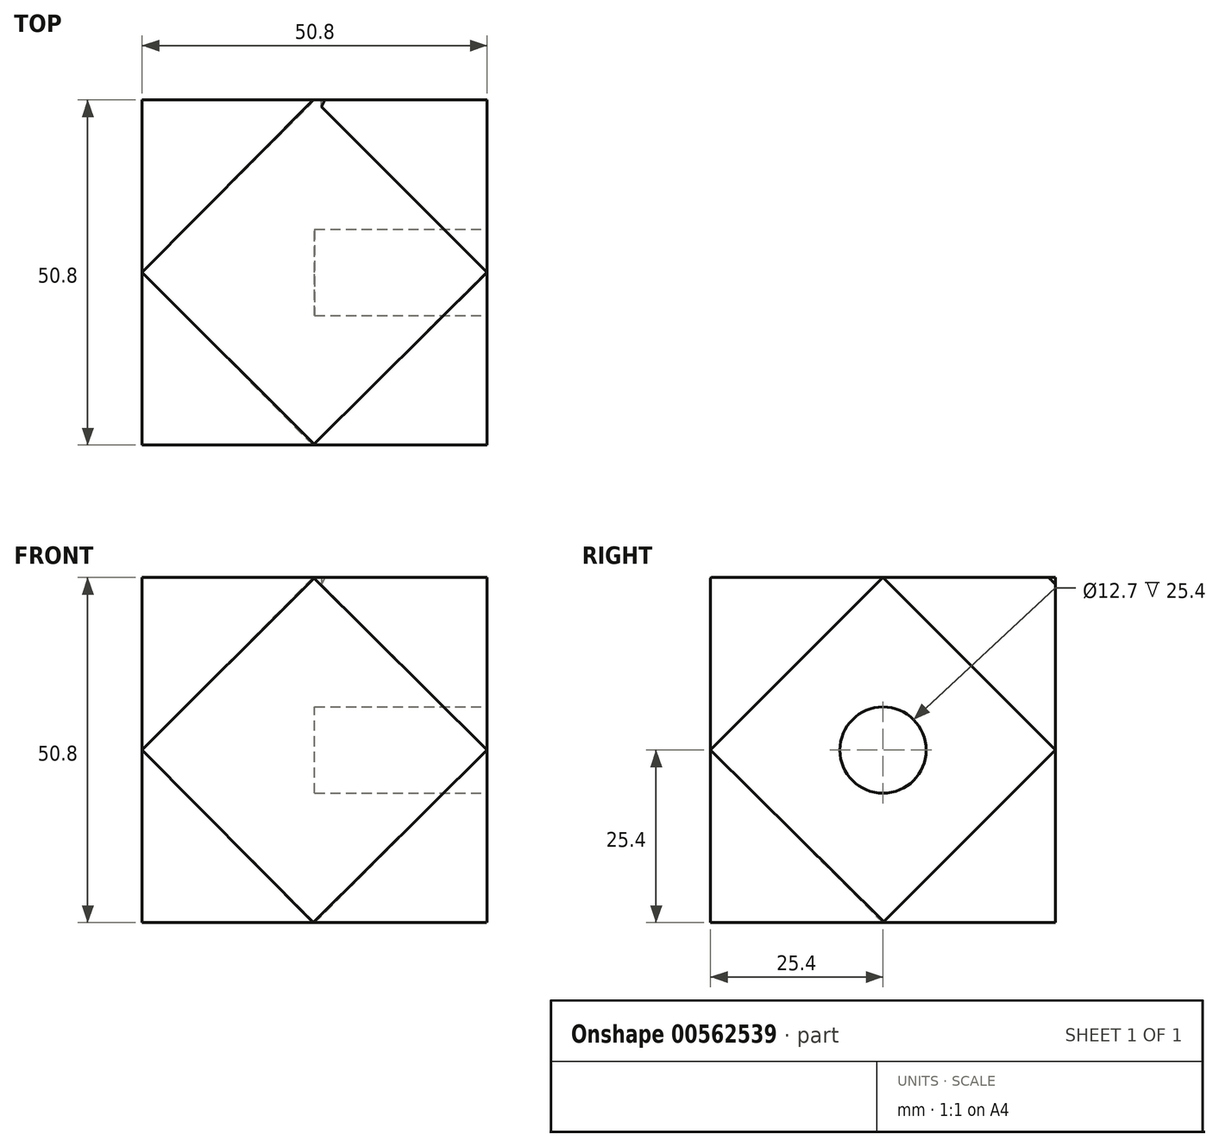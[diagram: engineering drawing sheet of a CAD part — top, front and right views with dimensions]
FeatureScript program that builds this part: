
annotation { "Feature Type Name" : "Feature", "Feature Type Description" : "" }
export const myFeature = defineFeature(function(context is Context, id is Id, definition is map)
    precondition{}
    {
        {
            var Q0;
            Q0=qCreatedBy(makeId("Front.planeOp"),FACE);
            var sketch = newSketch(context, id + "F0", { "sketchPlane" : qUnion([Q0])});
            skLineSegment(sketch, "E0.bottom", {"start": v(-25.15, 0) * mm, "end": v(25.65, 0) * mm});
            skLineSegment(sketch, "E0.top", {"start": v(-25.15, 50.8) * mm, "end": v(25.65, 50.8) * mm});
            skLineSegment(sketch, "E0.left", {"start": v(-25.15, 0) * mm, "end": v(-25.15, 50.8) * mm});
            skLineSegment(sketch, "E0.right", {"start": v(25.65, 0) * mm, "end": v(25.65, 50.8) * mm});
            skSolve(sketch);
        }
        {
            var Q0;
            Q0 = qSketchRegion(id + "F0", true);
            extrude(context, id + "F1", {"entities" : qUnion([Q0]), "endBound" : BoundingType.SYMMETRIC, "depth" : 50.8 * mm, "offsetDistance" : 25 * mm});
        }
        {
            var Q0;
            Q0=makeQuery(id+"F1.opExtrude","CAP_FACE",FACE,{"disambiguationData":[OSD([sQuery(id+"F0.wireOp",EDGE,"E0.bottom"),sQuery(id+"F0.wireOp",EDGE,"E0.top"),sQuery(id+"F0.wireOp",EDGE,"E0.left"),sQuery(id+"F0.wireOp",EDGE,"E0.right")])],"isStart":false});
            var sketch = newSketch(context, id + "F2", { "sketchPlane" : qUnion([Q0])});
            skLineSegment(sketch, "E1", {"start": v(25.65, 25.4) * mm, "end": v(0, 50.8) * mm});
            skLineSegment(sketch, "E2", {"start": v(0, 50.8) * mm, "end": v(-25.15, 25.4) * mm});
            skLineSegment(sketch, "E3", {"start": v(-25.15, 25.4) * mm, "end": v(0, 0) * mm});
            skLineSegment(sketch, "E4", {"start": v(0, 0) * mm, "end": v(25.65, 25.4) * mm});
            skSolve(sketch);
        }
        {
            var Q0;
            Q0=makeQuery(id+"F1.opExtrude","SWEPT_FACE",FACE,{"disambiguationData":[OSD([sQuery(id+"F0.wireOp",EDGE,"E0.right")])]});
            var sketch = newSketch(context, id + "F3", { "sketchPlane" : qUnion([Q0])});
            skLineSegment(sketch, "E5", {"start": v(0, 50.8) * mm, "end": v(-25.4, 25.4) * mm});
            skLineSegment(sketch, "E6", {"start": v(-25.4, 25.4) * mm, "end": v(0, 0) * mm});
            skLineSegment(sketch, "E7", {"start": v(0, 0) * mm, "end": v(25.4, 25.4) * mm});
            skLineSegment(sketch, "E8", {"start": v(25.4, 25.4) * mm, "end": v(0, 50.8) * mm});
            skSolve(sketch);
        }
        {
            var Q0;
            Q0=makeQuery(id+"F1.opExtrude","CAP_FACE",FACE,{"disambiguationData":[OSD([sQuery(id+"F0.wireOp",EDGE,"E0.bottom"),sQuery(id+"F0.wireOp",EDGE,"E0.top"),sQuery(id+"F0.wireOp",EDGE,"E0.left"),sQuery(id+"F0.wireOp",EDGE,"E0.right")])],"isStart":true});
            var sketch = newSketch(context, id + "F4", { "sketchPlane" : qUnion([Q0])});
            skLineSegment(sketch, "E9", {"start": v(0, 50.8) * mm, "end": v(-25.65, 25.4) * mm});
            skLineSegment(sketch, "E10", {"start": v(-25.65, 25.4) * mm, "end": v(0, 0) * mm});
            skLineSegment(sketch, "E11", {"start": v(0, 0) * mm, "end": v(25.15, 25.4) * mm});
            skLineSegment(sketch, "E12", {"start": v(25.15, 25.4) * mm, "end": v(0, 50.8) * mm});
            skSolve(sketch);
        }
        {
            var Q0;
            Q0=makeQuery(id+"F1.opExtrude","SWEPT_FACE",FACE,{"disambiguationData":[OSD([sQuery(id+"F0.wireOp",EDGE,"E0.left")])]});
            var sketch = newSketch(context, id + "F5", { "sketchPlane" : qUnion([Q0])});
            skLineSegment(sketch, "E13", {"start": v(-25.4, 25.4) * mm, "end": v(0, 50.8) * mm});
            skLineSegment(sketch, "E14", {"start": v(0, 50.8) * mm, "end": v(25.4, 25.4) * mm});
            skLineSegment(sketch, "E15", {"start": v(25.4, 25.4) * mm, "end": v(0, 0) * mm});
            skLineSegment(sketch, "E16", {"start": v(0, 0) * mm, "end": v(-25.4, 25.4) * mm});
            skSolve(sketch);
        }
        {
            var Q0;
            Q0=makeQuery(id+"F1.opExtrude","SWEPT_FACE",FACE,{"disambiguationData":[OSD([sQuery(id+"F0.wireOp",EDGE,"E0.top")])]});
            var sketch = newSketch(context, id + "F6", { "sketchPlane" : qUnion([Q0])});
            skLineSegment(sketch, "E17", {"start": v(-25.15, 0) * mm, "end": v(0.25, 25.4) * mm});
            skLineSegment(sketch, "E18", {"start": v(0.25, 25.4) * mm, "end": v(25.65, 0) * mm});
            skLineSegment(sketch, "E19", {"start": v(25.65, 0) * mm, "end": v(0.25, -25.4) * mm});
            skLineSegment(sketch, "E20", {"start": v(0.25, -25.4) * mm, "end": v(-25.15, 0) * mm});
            skSolve(sketch);
        }
        {
            var Q0;
            Q0=makeQuery(id+"F1.opExtrude","SWEPT_FACE",FACE,{"disambiguationData":[OSD([sQuery(id+"F0.wireOp",EDGE,"E0.bottom")])]});
            var sketch = newSketch(context, id + "F7", { "sketchPlane" : qUnion([Q0])});
            skLineSegment(sketch, "E21", {"start": v(-25.15, 0) * mm, "end": v(0.25, 25.4) * mm});
            skLineSegment(sketch, "E22", {"start": v(0.25, 25.4) * mm, "end": v(25.65, 0) * mm});
            skLineSegment(sketch, "E23", {"start": v(25.65, 0) * mm, "end": v(0.25, -25.4) * mm});
            skLineSegment(sketch, "E24", {"start": v(0.25, -25.4) * mm, "end": v(-25.15, 0) * mm});
            skSolve(sketch);
        }
        {
            var Q0;
            Q0=sQuery(id+"F7.wireOp",EDGE,"E24");
            var Q1;
            Q1=sQuery(id+"F5.wireOp",EDGE,"E16");
            cPlane(context, id + "F8", {"entities" : qUnion([Q0, Q1]), "cplaneType" : CPlaneType.LINE_ANGLE, "offset" : 25 * mm, "angle" : 0 * degree, "width" : 150 * mm, "height" : 150 * mm});
        }
        {
            var Q0;
            Q0=qCreatedBy(id+"F8.planeOp",FACE);
            var sketch = newSketch(context, id + "F9", { "sketchPlane" : qUnion([Q0])});
            skLineSegment(sketch, "E25.bottom", {"start": v(30.6, -24.4) * mm, "end": v(-50.97, -24.4) * mm});
            skLineSegment(sketch, "E25.top", {"start": v(30.6, 46.24) * mm, "end": v(-50.97, 46.24) * mm});
            skLineSegment(sketch, "E25.left", {"start": v(30.6, -24.4) * mm, "end": v(30.6, 46.24) * mm});
            skLineSegment(sketch, "E25.right", {"start": v(-50.97, -24.4) * mm, "end": v(-50.97, 46.24) * mm});
            skSolve(sketch);
        }
        {
            var Q0;
            Q0 = qSketchRegion(id + "F9", true);
            extrude(context, id + "F10", {"entities" : qUnion([Q0]), "operationType" : NewBodyOperationType.REMOVE, "depth" : 29.3 * mm, "offsetDistance" : 25 * mm});
        }
        {
            var Q0;
            Q0=sQuery(id+"F3.wireOp",EDGE,"E7");
            var Q1;
            Q1=sQuery(id+"F7.wireOp",EDGE,"E23");
            cPlane(context, id + "F11", {"entities" : qUnion([Q0, Q1]), "cplaneType" : CPlaneType.LINE_ANGLE, "offset" : 25 * mm, "angle" : 0 * degree, "width" : 150 * mm, "height" : 150 * mm});
        }
        {
            var Q0;
            Q0=qCreatedBy(id+"F11.planeOp",FACE);
            var sketch = newSketch(context, id + "F12", { "sketchPlane" : qUnion([Q0])});
            skCircle(sketch, "E26", {"center": v(-35.5, 68) * mm, "radius": 89.54 * mm});
            skSolve(sketch);
        }
        {
            var Q0;
            Q0 = qSketchRegion(id + "F12", true);
            extrude(context, id + "F13", {"entities" : qUnion([Q0]), "operationType" : NewBodyOperationType.REMOVE, "oppositeDirection" : true, "depth" : 25 * mm, "offsetDistance" : 25 * mm});
        }
        {
            var Q0;
            Q0=sQuery(id+"F6.wireOp",EDGE,"E18");
            var Q1;
            Q1=sQuery(id+"F3.wireOp",EDGE,"E8");
            cPlane(context, id + "F14", {"entities" : qUnion([Q0, Q1]), "cplaneType" : CPlaneType.LINE_ANGLE, "offset" : 25 * mm, "angle" : 0 * degree, "width" : 150 * mm, "height" : 150 * mm});
        }
        {
            var Q0;
            Q0=qCreatedBy(id+"F14.planeOp",FACE);
            var sketch = newSketch(context, id + "F15", { "sketchPlane" : qUnion([Q0])});
            skCircle(sketch, "E27", {"center": v(9.89, 17.48) * mm, "radius": 39.57 * mm});
            skSolve(sketch);
        }
        {
            var Q0;
            Q0 = qSketchRegion(id + "F15", true);
            extrude(context, id + "F16", {"entities" : qUnion([Q0]), "operationType" : NewBodyOperationType.REMOVE, "oppositeDirection" : true, "depth" : 41 * mm, "offsetDistance" : 25 * mm});
        }
        {
            var Q0;
            Q0=sQuery(id+"F5.wireOp",EDGE,"E13");
            var Q1;
            Q1=sQuery(id+"F4.wireOp",EDGE,"E12");
            cPlane(context, id + "F17", {"entities" : qUnion([Q0, Q1]), "cplaneType" : CPlaneType.LINE_ANGLE, "offset" : 25 * mm, "angle" : 0 * degree, "width" : 150 * mm, "height" : 150 * mm});
        }
        {
            var Q0;
            Q0=qCreatedBy(id+"F17.planeOp",FACE);
            var sketch = newSketch(context, id + "F18", { "sketchPlane" : qUnion([Q0])});
            skLineSegment(sketch, "E28.bottom", {"start": v(33.93, 48.82) * mm, "end": v(-24.66, 48.82) * mm});
            skLineSegment(sketch, "E28.top", {"start": v(33.93, -22.32) * mm, "end": v(-24.66, -22.32) * mm});
            skLineSegment(sketch, "E28.left", {"start": v(33.93, 48.82) * mm, "end": v(33.93, -22.32) * mm});
            skLineSegment(sketch, "E28.right", {"start": v(-24.66, 48.82) * mm, "end": v(-24.66, -22.32) * mm});
            skSolve(sketch);
        }
        {
            var Q0;
            Q0 = qSketchRegion(id + "F18", true);
            extrude(context, id + "F19", {"entities" : qUnion([Q0]), "operationType" : NewBodyOperationType.REMOVE, "depth" : 100 * mm, "offsetDistance" : 25 * mm});
        }
        {
            var Q0;
            Q0=sQuery(id+"F6.wireOp",EDGE,"E20");
            var Q1;
            Q1=sQuery(id+"F5.wireOp",EDGE,"E14");
            cPlane(context, id + "F20", {"entities" : qUnion([Q0, Q1]), "cplaneType" : CPlaneType.LINE_ANGLE, "offset" : 25 * mm, "angle" : 0 * degree, "width" : 150 * mm, "height" : 150 * mm});
        }
        {
            var Q0;
            Q0=qCreatedBy(id+"F20.planeOp",FACE);
            var sketch = newSketch(context, id + "F21", { "sketchPlane" : qUnion([Q0])});
            skLineSegment(sketch, "E29.bottom", {"start": v(47.9, 49.5) * mm, "end": v(-32.27, 49.5) * mm});
            skLineSegment(sketch, "E29.top", {"start": v(47.9, -6.14) * mm, "end": v(-32.27, -6.14) * mm});
            skLineSegment(sketch, "E29.left", {"start": v(47.9, 49.5) * mm, "end": v(47.9, -6.14) * mm});
            skLineSegment(sketch, "E29.right", {"start": v(-32.27, 49.5) * mm, "end": v(-32.27, -6.14) * mm});
            skSolve(sketch);
        }
        {
            var Q0;
            Q0 = qSketchRegion(id + "F21", true);
            extrude(context, id + "F22", {"entities" : qUnion([Q0]), "operationType" : NewBodyOperationType.REMOVE, "depth" : 42.7 * mm, "offsetDistance" : 25 * mm});
        }
        {
            var Q0;
            Q0=sQuery(id+"F2.wireOp",EDGE,"E3");
            var Q1;
            Q1=sQuery(id+"F5.wireOp",EDGE,"E15");
            cPlane(context, id + "F23", {"entities" : qUnion([Q0, Q1]), "cplaneType" : CPlaneType.LINE_ANGLE, "offset" : 25 * mm, "angle" : 0 * degree, "width" : 150 * mm, "height" : 150 * mm});
        }
        {
            var Q0;
            Q0=qCreatedBy(id+"F23.planeOp",FACE);
            var sketch = newSketch(context, id + "F24", { "sketchPlane" : qUnion([Q0])});
            skLineSegment(sketch, "E30.bottom", {"start": v(-58.44, 44.58) * mm, "end": v(29.21, 44.58) * mm});
            skLineSegment(sketch, "E30.top", {"start": v(-58.44, -24.22) * mm, "end": v(29.21, -24.22) * mm});
            skLineSegment(sketch, "E30.left", {"start": v(-58.44, 44.58) * mm, "end": v(-58.44, -24.22) * mm});
            skLineSegment(sketch, "E30.right", {"start": v(29.21, 44.58) * mm, "end": v(29.21, -24.22) * mm});
            skSolve(sketch);
        }
        {
            var Q0;
            Q0 = qSketchRegion(id + "F24", true);
            extrude(context, id + "F25", {"entities" : qUnion([Q0]), "operationType" : NewBodyOperationType.REMOVE, "oppositeDirection" : true, "depth" : 25 * mm, "offsetDistance" : 25 * mm});
        }
        {
            var Q0;
            Q0=sQuery(id+"F2.wireOp",EDGE,"E4");
            var Q1;
            Q1=sQuery(id+"F7.wireOp",EDGE,"E22");
            cPlane(context, id + "F26", {"entities" : qUnion([Q0, Q1]), "cplaneType" : CPlaneType.LINE_ANGLE, "offset" : 25 * mm, "angle" : 0 * degree, "width" : 150 * mm, "height" : 150 * mm});
        }
        {
            var Q0;
            Q0=qCreatedBy(id+"F26.planeOp",FACE);
            var sketch = newSketch(context, id + "F27", { "sketchPlane" : qUnion([Q0])});
            skLineSegment(sketch, "E31.bottom", {"start": v(51.14, -63.43) * mm, "end": v(-48.87, -63.43) * mm});
            skLineSegment(sketch, "E31.top", {"start": v(51.14, 53.58) * mm, "end": v(-48.87, 53.58) * mm});
            skLineSegment(sketch, "E31.left", {"start": v(51.14, -63.43) * mm, "end": v(51.14, 53.58) * mm});
            skLineSegment(sketch, "E31.right", {"start": v(-48.87, -63.43) * mm, "end": v(-48.87, 53.58) * mm});
            skSolve(sketch);
        }
        {
            var Q0;
            Q0 = qSketchRegion(id + "F27", true);
            extrude(context, id + "F28", {"entities" : qUnion([Q0]), "operationType" : NewBodyOperationType.REMOVE, "oppositeDirection" : true, "depth" : 25 * mm, "offsetDistance" : 25 * mm});
        }
        {
            var Q0;
            Q0=sQuery(id+"F2.wireOp",EDGE,"E1");
            var Q1;
            Q1=sQuery(id+"F3.wireOp",EDGE,"E5");
            cPlane(context, id + "F29", {"entities" : qUnion([Q0, Q1]), "cplaneType" : CPlaneType.LINE_ANGLE, "offset" : 25 * mm, "angle" : 0 * degree, "width" : 150 * mm, "height" : 150 * mm});
        }
        {
            var Q0;
            Q0=qCreatedBy(id+"F29.planeOp",FACE);
            var sketch = newSketch(context, id + "F30", { "sketchPlane" : qUnion([Q0])});
            skLineSegment(sketch, "E32.bottom", {"start": v(-67.2, 18.75) * mm, "end": v(53.33, 18.75) * mm});
            skLineSegment(sketch, "E32.top", {"start": v(-67.2, -9.42) * mm, "end": v(53.33, -9.42) * mm});
            skLineSegment(sketch, "E32.left", {"start": v(-67.2, 18.75) * mm, "end": v(-67.2, -9.42) * mm});
            skLineSegment(sketch, "E32.right", {"start": v(53.33, 18.75) * mm, "end": v(53.33, -9.42) * mm});
            skLineSegment(sketch, "E33.bottom", {"start": v(-45.4, 42.47) * mm, "end": v(35.79, 42.47) * mm});
            skLineSegment(sketch, "E33.top", {"start": v(-45.4, 18.75) * mm, "end": v(35.79, 18.75) * mm});
            skLineSegment(sketch, "E33.left", {"start": v(-45.4, 42.47) * mm, "end": v(-45.4, 18.75) * mm});
            skLineSegment(sketch, "E33.right", {"start": v(35.79, 42.47) * mm, "end": v(35.79, 18.75) * mm});
            skLineSegment(sketch, "E34.bottom", {"start": v(35.54, 19.43) * mm, "end": v(35.79, 19.43) * mm});
            skLineSegment(sketch, "E34.top", {"start": v(35.54, 22.12) * mm, "end": v(35.79, 22.12) * mm});
            skLineSegment(sketch, "E34.left", {"start": v(35.54, 19.43) * mm, "end": v(35.54, 22.12) * mm});
            skLineSegment(sketch, "E34.right", {"start": v(35.79, 19.43) * mm, "end": v(35.79, 22.12) * mm});
            skSolve(sketch);
        }
        {
            var Q0;
            {var subQ1=sQuery(id+"F30.wireOp",EDGE,"E33.bottom");var subQ9=sQuery(id+"F30.wireOp",EDGE,"E34.bottom");var subQ10=makeQuery(id+"F30.imprint","IMPRINT",EDGE,{"derivedFrom":subQ9});Q0=qUnion([makeQuery(id+"F30.imprint","IMPRINT",FACE,{"disambiguationData":[TD([[makeQuery(id+"F30.imprint","IMPRINT",EDGE,{"derivedFrom":sQuery(id+"F30.wireOp",EDGE,"E32.top")}),1.0]])]}),makeQuery(id+"F30.imprint","IMPRINT",FACE,{"disambiguationData":[TD([[subQ10,1.0]])]}),makeQuery(id+"F30.imprint","IMPRINT",FACE,{"disambiguationData":[TD([[makeQuery(id+"F30.imprint","IMPRINT",EDGE,{"derivedFrom":subQ1}),-1.0]])]})]);}
            extrude(context, id + "F31", {"entities" : qUnion([Q0]), "operationType" : NewBodyOperationType.REMOVE, "depth" : 48.9 * mm, "offsetDistance" : 25 * mm});
        }
        {
            var Q0;
            Q0=makeQuery(id+"F3.imprint","IMPRINT",FACE,{"disambiguationData":[TD([[makeQuery(id+"F3.imprint","IMPRINT",EDGE,{"derivedFrom":sQuery(id+"F3.wireOp",EDGE,"E5")}),1.0]])]});
            var sketch = newSketch(context, id + "F32", { "sketchPlane" : qUnion([Q0])});
            skCircle(sketch, "E35", {"center": v(0, 25.4) * mm, "radius": 6.35 * mm});
            skSolve(sketch);
        }
        {
            var Q0;
            Q0=makeQuery(id+"F32.imprint","IMPRINT",FACE,{"disambiguationData":[TD([[makeQuery(id+"F32.imprint","IMPRINT",EDGE,{"derivedFrom":sQuery(id+"F32.wireOp",EDGE,"E35")}),1.0]])]});
            extrude(context, id + "F33", {"entities" : qUnion([Q0]), "operationType" : NewBodyOperationType.REMOVE, "oppositeDirection" : true, "depth" : 25.4 * mm, "offsetDistance" : 25 * mm});
        }
    });
